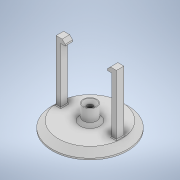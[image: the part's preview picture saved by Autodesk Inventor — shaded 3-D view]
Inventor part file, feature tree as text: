
AUTODESK INVENTOR PART (.ipt)
format: ipt  version: 2020.4 (Build 244396000, 396)  size: 167,936 bytes
history: native  units: in
note: dims shown in document units (in); Inventor stores cm internally (conversion verified against a paired STEP export)
features: chamfer x5, extrude x4, sketch x4, mirror x1
ambient origin geometry x8: Origin, YZ Plane, XZ Plane, XY Plane, X Axis, Y Axis, Z Axis, Center Point
bodies: Solid1 (feature_tree)
feature tree (14):
  extrude  "Extrusion1"  Depth=0.1969in TaperAngle=0.0deg
  chamfer  "Chamfer1"  Distance=0.0787in Angle=45.0deg
  extrude  "Extrusion2"  Depth=0.0787in
  chamfer  "Chamfer2"  Distance=0.3937in
  chamfer  "Chamfer3"  Distance=0.0787in Angle=45.0deg
  extrude  "Extrusion3"  Depth=0.1181in
  extrude  "Extrusion4"  Depth=1.5748in TaperAngle=0.0deg
  chamfer  "Chamfer4"  Distance=0.1181in
  mirror  "Mirror1"
  chamfer  "Chamfer6"  Distance=0.1181in
  sketch  "Sketch1"  dims[d0=1.9685in d1=0.1969in d2=0.0in d3=0.1575in d4=0.0787in d5=45.0deg]
  sketch  "Sketch2"  dims[d6=0.1575in d7=0.3543in d8=0.3937in d9=0.0in d10=0.0787in d11=0.0787in d12=45.0deg]
  sketch  "Sketch3"  dims[d13=0.0787in d14=0.0787in d15=45.0deg d16=0.1181in]
  sketch  "Sketch4"  dims[d17=0.1969in d18=1.5748in d19=0.0in d20=0.1181in d21=0.1181in d22=0.0in d23=0.0787in d24=0.0787in d25=45.0deg d29=0.6693in d30=0.0197in d31=0.0787in d32=45.0deg]
